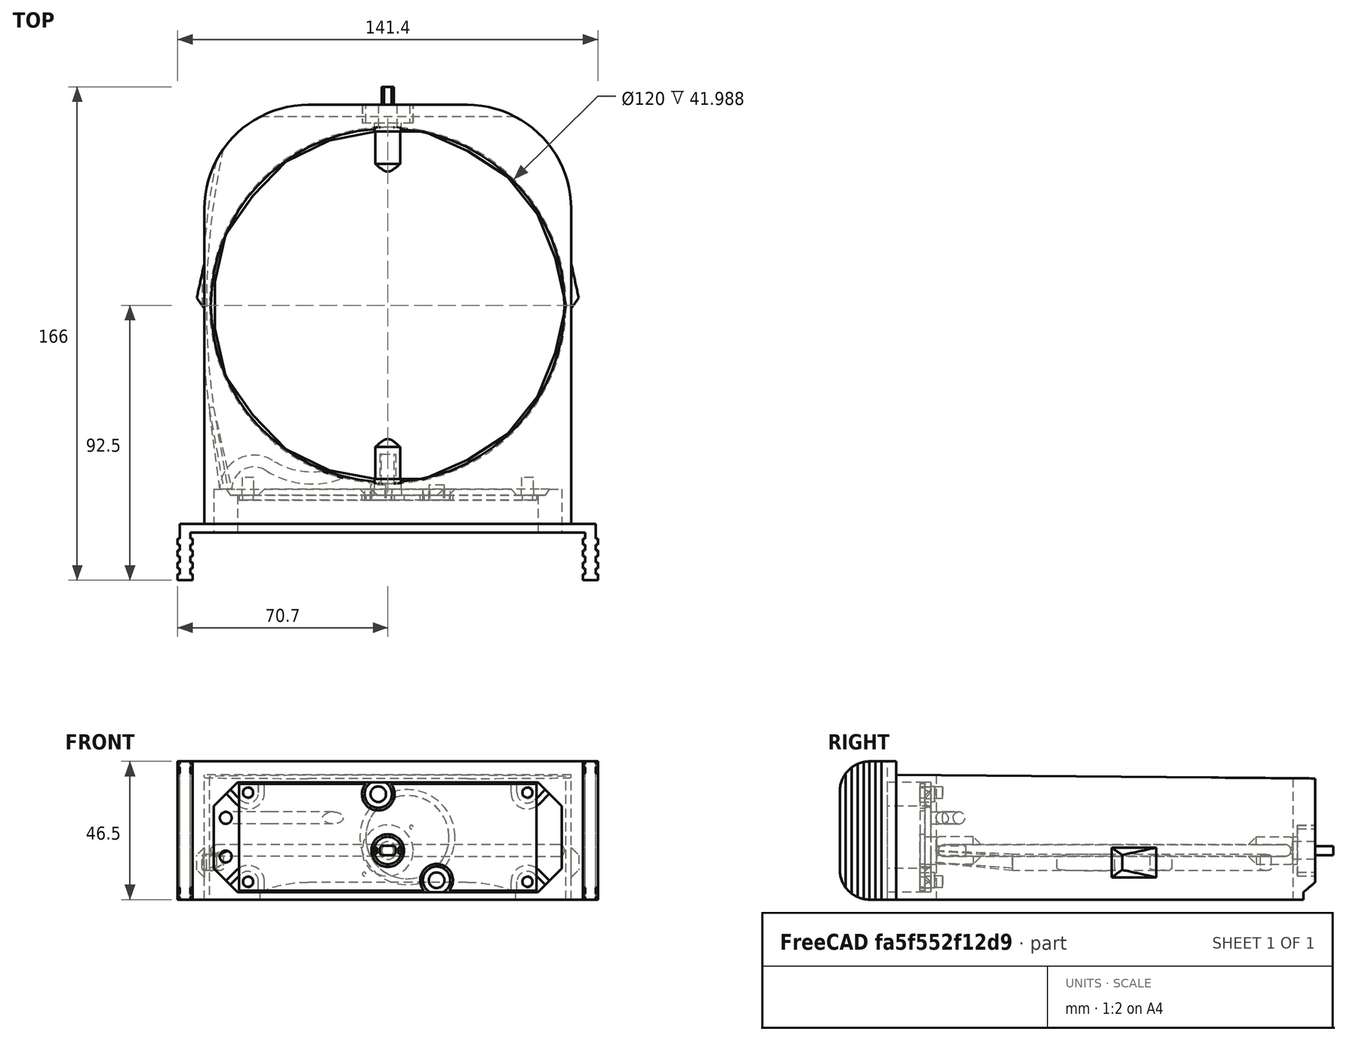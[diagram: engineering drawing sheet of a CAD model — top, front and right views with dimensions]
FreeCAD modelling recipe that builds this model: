
FCSTD DOCUMENT  (FreeCAD 0.20R27936 (Git))
Label: OpenDucoValve
License: All rights reserved
LicenseURL: http://en.wikipedia.org/wiki/All_rights_reserved
objects: Sketcher::SketchObject×26, TechDraw::DrawViewDimension×16, PartDesign::Pad×8, PartDesign::Pocket×8, PartDesign::Plane×5, PartDesign::Body×3, PartDesign::Line×2, PartDesign::Mirrored×2, PartDesign::SubtractivePipe×2, PartDesign::Fillet×2, PartDesign::Chamfer×2, Spreadsheet::Sheet×1, PartDesign::AdditiveLoft×1, PartDesign::SubtractiveLoft×1, TechDraw::DrawSVGTemplate×1, TechDraw::DrawViewPart×1, TechDraw::DrawPage×1
note: 86 computed .brp shape members not serialized (recipe doc carries the construction recipe); baked Part::Feature solids carry a one-line shape summary decoded from their .brp

FEATURE [Spreadsheet::Sheet] Spreadsheet
  cells = A1=Bearing Bore Size; B1(BearingBoreSize)=17.2; A2=Threaded Insert M4 Hole Size; B2(ThreadedInsertM4HoleSize)=5.25; C2=M4 X D6.0 X L5.0; A3=PCB Screw Hole Size; B3(ThreadedInsertM3HoleSize)=3.95; C3=M3 X D5.0 X L5.0; D3=3.95; A4=Motor Shaft Cutout Diameter; B4(MotorShaftCutoutDiameter)=5.4; A5=Motor Shaft Cutout Thickness; B5(MotorShaftCutoutThickness)=3.1; A6=Potentiometer Pin Diameter; B6(PotentiometerPinDiameter)=4; A7=Potentiometer Pin Thickness; B7(PotentiometerPinThickness)=3; A8=Bearing Inside Bore Size; B8(BearingInsideBoreSize)=6; A9=PCB Thickness; B9(PCBThickness)=1.6; C9=PCB Size 100x36; D9=Hole Square 94x30
FEATURE [Sketcher::SketchObject] Sketch
  FullyConstrained = true
  MapMode = 5
  Support = -> [XY_Plane]
  sketch-geometry (71):
    g0: Circle CenterX=0 CenterY=0 CenterZ=0 NormalX=0 NormalY=0 NormalZ=1 AngleXU=0 Radius=60
    g1: LineSegment StartX=-61.75 StartY=-73.5 StartZ=0 EndX=-61.75 EndY=32.5 EndZ=0
    g2: LineSegment StartX=61.75 StartY=-73.5 StartZ=0 EndX=61.75 EndY=32.5 EndZ=0
    g3: LineSegment StartX=26.75 StartY=67.5 StartZ=0 EndX=-26.75 EndY=67.5 EndZ=0
    g4: ArcOfCircle CenterX=-26.75 CenterY=32.5 CenterZ=0 NormalX=0 NormalY=0 NormalZ=1 AngleXU=0 Radius=35 StartAngle=1.5708 EndAngle=3.14159
    g5: ArcOfCircle CenterX=26.75 CenterY=32.5 CenterZ=0 NormalX=0 NormalY=0 NormalZ=1 AngleXU=0 Radius=35 StartAngle=0 EndAngle=1.5708
    g6: LineSegment StartX=-61.75 StartY=-73.5 StartZ=0 EndX=-70 EndY=-73.5 EndZ=0
    g7: LineSegment StartX=61.75 StartY=-73.5 StartZ=0 EndX=70 EndY=-73.5 EndZ=0
    g8: LineSegment StartX=-70 StartY=-73.5 StartZ=0 EndX=-70 EndY=-78.5 EndZ=0
    g9: LineSegment StartX=-70 StartY=-78.5 StartZ=0 EndX=-70.7 EndY=-78.5 EndZ=0
    g10: LineSegment StartX=-70.7 StartY=-78.5 StartZ=0 EndX=-70.7 EndY=-80.5 EndZ=0
    g11: LineSegment StartX=-70.7 StartY=-80.5 StartZ=0 EndX=-70 EndY=-80.5 EndZ=0
    g12: LineSegment StartX=-70 StartY=-80.5 StartZ=0 EndX=-70 EndY=-82.5 EndZ=0
    g13: LineSegment StartX=-70 StartY=-82.5 StartZ=0 EndX=-70.7 EndY=-82.5 EndZ=0
    g14: LineSegment StartX=-70.7 StartY=-82.5 StartZ=0 EndX=-70.7 EndY=-84.5 EndZ=0
    g15: LineSegment StartX=-70.7 StartY=-84.5 StartZ=0 EndX=-70 EndY=-84.5 EndZ=0
    g16: LineSegment StartX=-70 StartY=-84.5 StartZ=0 EndX=-70 EndY=-86.5 EndZ=0
    g17: LineSegment StartX=-70 StartY=-86.5 StartZ=0 EndX=-70.7 EndY=-86.5 EndZ=0
    g18: LineSegment StartX=-70.7 StartY=-86.5 StartZ=0 EndX=-70.7 EndY=-88.5 EndZ=0
    g19: LineSegment StartX=-70.7 StartY=-88.5 StartZ=0 EndX=-70 EndY=-88.5 EndZ=0
    g20: LineSegment StartX=-70 StartY=-88.5 StartZ=0 EndX=-70 EndY=-90.5 EndZ=0
    g21: LineSegment StartX=-70 StartY=-90.5 StartZ=0 EndX=-70.7 EndY=-90.5 EndZ=0
    g22: LineSegment StartX=-70.7 StartY=-90.5 StartZ=0 EndX=-70.7 EndY=-92.5 EndZ=0
    g23: LineSegment StartX=-70.7 StartY=-92.5 StartZ=0 EndX=-65.7 EndY=-92.5 EndZ=0
    g24: LineSegment StartX=-65.7 StartY=-92.5 StartZ=0 EndX=-65.7 EndY=-90.5 EndZ=0
    g25: LineSegment StartX=-65.7 StartY=-90.5 StartZ=0 EndX=-66.4 EndY=-90.5 EndZ=0
    g26: LineSegment StartX=-66.4 StartY=-90.5 StartZ=0 EndX=-66.4 EndY=-88.5 EndZ=0
    g27: LineSegment StartX=-66.4 StartY=-88.5 StartZ=0 EndX=-65.7 EndY=-88.5 EndZ=0
    g28: LineSegment StartX=-65.7 StartY=-88.5 StartZ=0 EndX=-65.7 EndY=-86.5 EndZ=0
    g29: LineSegment StartX=-65.7 StartY=-86.5 StartZ=0 EndX=-66.4 EndY=-86.5 EndZ=0
    g30: LineSegment StartX=-66.4 StartY=-86.5 StartZ=0 EndX=-66.4 EndY=-84.5 EndZ=0
    g31: LineSegment StartX=-66.4 StartY=-84.5 StartZ=0 EndX=-65.7 EndY=-84.5 EndZ=0
    g32: LineSegment StartX=-65.7 StartY=-84.5 StartZ=0 EndX=-65.7 EndY=-82.5 EndZ=0
    g33: LineSegment StartX=-65.7 StartY=-82.5 StartZ=0 EndX=-66.4 EndY=-82.5 EndZ=0
    g34: LineSegment StartX=-66.4 StartY=-82.5 StartZ=0 EndX=-66.4 EndY=-80.5 EndZ=0
    g35: LineSegment StartX=-66.4 StartY=-80.5 StartZ=0 EndX=-65.7 EndY=-80.5 EndZ=0
    g36: LineSegment StartX=-66.4 StartY=-76.5 StartZ=0 EndX=66.4 EndY=-76.5 EndZ=0
    g37: LineSegment StartX=-65.7 StartY=-80.5 StartZ=0 EndX=-65.7 EndY=-78.5 EndZ=0
    g38: LineSegment StartX=-65.7 StartY=-78.5 StartZ=0 EndX=-66.4 EndY=-78.5 EndZ=0
    g39: LineSegment StartX=-66.4 StartY=-78.5 StartZ=0 EndX=-66.4 EndY=-76.5 EndZ=0
    g40: LineSegment StartX=70 StartY=-73.5 StartZ=0 EndX=70 EndY=-78.5 EndZ=0
    g41: LineSegment StartX=70 StartY=-78.5 StartZ=0 EndX=70.7 EndY=-78.5 EndZ=0
    g42: LineSegment StartX=70.7 StartY=-78.5 StartZ=0 EndX=70.7 EndY=-80.5 EndZ=0
    g43: LineSegment StartX=70.7 StartY=-80.5 StartZ=0 EndX=70 EndY=-80.5 EndZ=0
    g44: LineSegment StartX=70 StartY=-80.5 StartZ=0 EndX=70 EndY=-82.5 EndZ=0
    g45: LineSegment StartX=70 StartY=-82.5 StartZ=0 EndX=70.7 EndY=-82.5 EndZ=0
    g46: LineSegment StartX=70.7 StartY=-82.5 StartZ=0 EndX=70.7 EndY=-84.5 EndZ=0
    g47: LineSegment StartX=70.7 StartY=-84.5 StartZ=0 EndX=70 EndY=-84.5 EndZ=0
    g48: LineSegment StartX=70 StartY=-84.5 StartZ=0 EndX=70 EndY=-86.5 EndZ=0
    g49: LineSegment StartX=70 StartY=-86.5 StartZ=0 EndX=70.7 EndY=-86.5 EndZ=0
    g50: LineSegment StartX=70.7 StartY=-86.5 StartZ=0 EndX=70.7 EndY=-88.5 EndZ=0
    g51: LineSegment StartX=70.7 StartY=-88.5 StartZ=0 EndX=70 EndY=-88.5 EndZ=0
    g52: LineSegment StartX=70 StartY=-88.5 StartZ=0 EndX=70 EndY=-90.5001 EndZ=0
    g53: LineSegment StartX=70 StartY=-90.5001 StartZ=0 EndX=70.7 EndY=-90.5001 EndZ=0
    g54: LineSegment StartX=70.7 StartY=-90.5001 StartZ=0 EndX=70.7 EndY=-92.5001 EndZ=0
    g55: LineSegment StartX=70.7 StartY=-92.5001 StartZ=0 EndX=65.7 EndY=-92.5001 EndZ=0
    g56: LineSegment StartX=65.7 StartY=-92.5001 StartZ=0 EndX=65.7 EndY=-90.5001 EndZ=0
    g57: LineSegment StartX=65.7 StartY=-90.5001 StartZ=0 EndX=66.4 EndY=-90.5001 EndZ=0
    g58: LineSegment StartX=66.4 StartY=-90.5001 StartZ=0 EndX=66.4 EndY=-88.5 EndZ=0
    g59: LineSegment StartX=66.4 StartY=-88.5 StartZ=0 EndX=65.7 EndY=-88.5 EndZ=0
    g60: LineSegment StartX=65.7 StartY=-88.5 StartZ=0 EndX=65.7 EndY=-86.5 EndZ=0
    g61: LineSegment StartX=65.7 StartY=-86.5 StartZ=0 EndX=66.4 EndY=-86.5 EndZ=0
    g62: LineSegment StartX=66.4 StartY=-86.5 StartZ=0 EndX=66.4 EndY=-84.5 EndZ=0
    g63: LineSegment StartX=66.4 StartY=-84.5 StartZ=0 EndX=65.7 EndY=-84.5 EndZ=0
    g64: LineSegment StartX=65.7 StartY=-84.5 StartZ=0 EndX=65.7 EndY=-82.5 EndZ=0
    g65: LineSegment StartX=65.7 StartY=-82.5 StartZ=0 EndX=66.4 EndY=-82.5 EndZ=0
    g66: LineSegment StartX=66.4 StartY=-82.5 StartZ=0 EndX=66.4 EndY=-80.5 EndZ=0
    g67: LineSegment StartX=66.4 StartY=-80.5 StartZ=0 EndX=65.7 EndY=-80.5 EndZ=0
    g68: LineSegment StartX=65.7 StartY=-80.5 StartZ=0 EndX=65.7 EndY=-78.5 EndZ=0
    g69: LineSegment StartX=65.7 StartY=-78.5 StartZ=0 EndX=66.4 EndY=-78.5 EndZ=0
    g70: LineSegment StartX=66.4 StartY=-78.5 StartZ=0 EndX=66.4 EndY=-76.5 EndZ=0
  constraints (207):
    c: Coincident(g0,g-1)
    c: Diameter(g0) = 120
    c: Vertical(g1)
    c: Vertical(g2)
    c: Tangent(g1,g4) = 1.5708
    c: Tangent(g3,g4) = -1.5708
    c: Tangent(g2,g5) = -1.5708
    c: Tangent(g3,g5) = -1.5708
    c: Radius(g5) = 35
    c: DistanceY(g0,g3) = 67.5
    c: Symmetric(g3,g3,g-2)
    c: DistanceX(g1,g2) = 123.5
    c: DistanceY(g1,g0) = 73.5
    c: Symmetric(g1,g2,g-2)
    c: Coincident(g6,g1)
    c: Horizontal(g6)
    c: Coincident(g7,g2)
    c: Horizontal(g7)
    c: Equal(g7,g6)
    c: DistanceX(g6,g7) = 140
    c: Coincident(g8,g6)
    c: Vertical(g8)
    c: Coincident(g9,g8)
    c: Horizontal(g9)
    c: Coincident(g10,g9)
    c: Vertical(g10)
    c: Coincident(g11,g10)
    c: Horizontal(g11)
    c: Coincident(g12,g11)
    c: Vertical(g12)
    c: Coincident(g13,g12)
    c: Horizontal(g13)
    c: Coincident(g14,g13)
    c: Vertical(g14)
    c: Coincident(g15,g14)
    c: Horizontal(g15)
    c: Coincident(g16,g15)
    c: Vertical(g16)
    c: Coincident(g17,g16)
    c: Horizontal(g17)
    c: Coincident(g18,g17)
    c: Vertical(g18)
    c: Coincident(g19,g18)
    c: Coincident(g20,g19)
    c: Vertical(g20)
    c: Coincident(g21,g20)
    c: Horizontal(g21)
    c: Coincident(g22,g21)
    c: Vertical(g22)
    c: Vertical(g8,g15)
    c: Vertical(g15,g19)
    c: Vertical(g9,g13)
    c: Vertical(g13,g17)
    c: Vertical(g17,g21)
    c: Equal(g22,g20)
    c: Equal(g20,g18)
    c: Equal(g18,g16)
    c: Equal(g16,g14)
    c: Equal(g14,g12)
    c: Equal(g12,g10)
    c: Equal(g19,g17)
    c: Equal(g15,g13)
    c: DistanceX(g9,g9) = 0.7
    c: DistanceY(g10,g10) = 2
    c: Coincident(g23,g22)
    c: Horizontal(g23)
    c: Coincident(g24,g23)
    c: Vertical(g24)
    c: Coincident(g25,g24)
    c: Horizontal(g25)
    c: Coincident(g26,g25)
    c: Vertical(g26)
    c: Coincident(g26,g27)
    c: Horizontal(g27)
    c: Coincident(g27,g28)
    c: Vertical(g28)
    c: Coincident(g28,g29)
    c: Horizontal(g29)
    c: Coincident(g29,g30)
    c: Vertical(g30)
    c: Coincident(g30,g31)
    c: Horizontal(g31)
    c: Coincident(g31,g32)
    c: Vertical(g32)
    c: Coincident(g32,g33)
    c: Horizontal(g33)
    c: Coincident(g33,g34)
    c: Vertical(g34)
    c: Coincident(g34,g35)
    c: Horizontal(g35)
    c: Horizontal(g21,g24)
    c: Horizontal(g27,g18)
    c: Horizontal(g28,g17)
    c: Horizontal(g31,g14)
    c: Horizontal(g32,g13)
    c: Horizontal(g35,g10)
    c: Vertical(g25,g29)
    c: Vertical(g29,g33)
    c: Vertical(g24,g27)
    c: Vertical(g27,g31)
    c: Vertical(g31,g35)
    c: Equal(g13,g33)
    c: DistanceX(g23,g23) = 5
    c: Symmetric(g36,g36,g-2)
    c: DistanceY(g36,g1) = 3
    c: Coincident(g35,g37)
    c: Vertical(g37)
    c: Coincident(g37,g38)
    c: Coincident(g38,g39)
    c: Coincident(g39,g36)
    c: Vertical(g39)
    c: Horizontal(g38)
    c: Vertical(g38,g34)
    c: Horizontal(g37,g8)
    c: Equal(g37,g39)
    c: Vertical(g40)
    c: Coincident(g41,g40)
    c: Horizontal(g41)
    c: Coincident(g42,g41)
    c: Vertical(g42)
    c: Coincident(g43,g42)
    c: Horizontal(g43)
    c: Coincident(g44,g43)
    c: Vertical(g44)
    c: Coincident(g45,g44)
    c: Horizontal(g45)
    c: Coincident(g46,g45)
    c: Vertical(g46)
    c: Coincident(g47,g46)
    c: Horizontal(g47)
    c: Coincident(g48,g47)
    c: Vertical(g48)
    c: Coincident(g49,g48)
    c: Horizontal(g49)
    c: Coincident(g50,g49)
    c: Vertical(g50)
    c: Coincident(g51,g50)
    c: Coincident(g52,g51)
    c: Vertical(g52)
    c: Coincident(g53,g52)
    c: Horizontal(g53)
    c: Coincident(g54,g53)
    c: Vertical(g54)
    c: Equal(g54,g52)
    c: Equal(g52,g50)
    c: Equal(g50,g48)
    c: Equal(g48,g46)
    c: Equal(g46,g44)
    c: Equal(g44,g42)
    c: Equal(g51,g49)
    c: Coincident(g55,g54)
    c: Horizontal(g55)
    c: Coincident(g56,g55)
    c: Vertical(g56)
    c: Coincident(g57,g56)
    c: Horizontal(g57)
    c: Coincident(g58,g57)
    c: Vertical(g58)
    c: Coincident(g58,g59)
    c: Horizontal(g59)
    c: Coincident(g59,g60)
    c: Vertical(g60)
    c: Coincident(g60,g61)
    c: Horizontal(g61)
    c: Coincident(g61,g62)
    c: Vertical(g62)
    c: Coincident(g62,g63)
    c: Horizontal(g63)
    c: Coincident(g63,g64)
    c: Vertical(g64)
    c: Coincident(g64,g65)
    c: Horizontal(g65)
    c: Coincident(g65,g66)
    c: Vertical(g66)
    c: Coincident(g66,g67)
    c: Horizontal(g67)
    c: Equal(g45,g65)
    c: Coincident(g67,g68)
    c: Vertical(g68)
    c: Coincident(g68,g69)
    c: Coincident(g69,g70)
    c: Vertical(g70)
    c: Horizontal(g69)
    c: Equal(g68,g70)
    c: Coincident(g70,g36)
    c: Equal(g58,g60)
    c: Equal(g60,g62)
    c: Equal(g62,g64)
    c: Equal(g64,g66)
    c: Equal(g66,g68)
    c: Equal(g70,g56)
    c: Equal(g56,g54)
    c: Equal(g69,g67)
    c: Equal(g67,g65)
    c: Equal(g65,g63)
    c: Equal(g63,g61)
    c: Equal(g61,g59)
    c: Equal(g59,g57)
    c: Equal(g57,g53)
    c: Equal(g53,g51)
    c: Equal(g49,g47)
    c: Equal(g45,g43)
    c: Equal(g43,g41)
    c: Coincident(g40,g7)
    c: Horizontal(g51)
    c: Equal(g63,g29)
    c: Equal(g56,g26)
FEATURE [PartDesign::Pad] Pad
  Direction = (0,0,1)
  Length = 46.5
  Length2 = 10
  Profile = -> Sketch
  ReferenceAxis = -> Sketch [N_Axis]
  Type = 0
FEATURE [Sketcher::SketchObject] Sketch001
  FullyConstrained = true
  MapMode = 5
  Placement = pos=(0,0,0) rot=(0.57735,0.57735,0.57735;2.0944rad)
  Support = -> [YZ_Plane]
  sketch-geometry (16):
    g0: LineSegment StartX=-73.5 StartY=46.5 StartZ=0 EndX=-73.5 EndY=42 EndZ=0
    g1: LineSegment StartX=-73.5 StartY=42 StartZ=0 EndX=67.5 EndY=40.7695 EndZ=0
    g2: LineSegment StartX=67.5 StartY=40.7695 StartZ=0 EndX=67.5 EndY=46.5 EndZ=0
    g3: LineSegment StartX=-73.5 StartY=46.5 StartZ=0 EndX=67.5 EndY=46.5 EndZ=0
    g4: LineSegment StartX=63.5 StartY=0 StartZ=0 EndX=63.5 EndY=2.5 EndZ=0
    g5: LineSegment StartX=63.5 StartY=2.5 StartZ=0 EndX=67.5 EndY=5.8564 EndZ=0
    g6: LineSegment StartX=67.5 StartY=5.8564 StartZ=0 EndX=67.5 EndY=0 EndZ=0
    g7: LineSegment StartX=67.5 StartY=0 StartZ=0 EndX=63.5 EndY=0 EndZ=0
    g8: ArcOfCircle CenterX=-82.5 CenterY=36.5 CenterZ=0 NormalX=0 NormalY=0 NormalZ=1 AngleXU=0 Radius=10 StartAngle=1.5708 EndAngle=3.14159
    g9: ArcOfCircle CenterX=-82.5 CenterY=10 CenterZ=0 NormalX=0 NormalY=0 NormalZ=1 AngleXU=0 Radius=10 StartAngle=3.14159 EndAngle=4.71239
    g10: LineSegment StartX=-92.5 StartY=36.5 StartZ=0 EndX=-92.5 EndY=10 EndZ=0
    g11: LineSegment StartX=-82.5 StartY=46.5 StartZ=0 EndX=-82.5 EndY=51 EndZ=0
    g12: LineSegment StartX=-82.5 StartY=51 StartZ=0 EndX=-223.5 EndY=51 EndZ=0
    g13: LineSegment StartX=-223.5 StartY=51 StartZ=0 EndX=-223.5 EndY=-4.5 EndZ=0
    g14: LineSegment StartX=-223.5 StartY=-4.5 StartZ=0 EndX=-82.5 EndY=-4.5 EndZ=0
    g15: LineSegment StartX=-82.5 StartY=-4.5 StartZ=0 EndX=-82.5 EndY=1.8e-15 EndZ=0
  constraints (50):
    c: Vertical(g0)
    c: Coincident(g1,g0)
    c: Coincident(g2,g1)
    c: Vertical(g2)
    c: Coincident(g3,g0)
    c: Coincident(g3,g2)
    c: DistanceY(g-1,g0) = 42
    c: DistanceX(g0,g-1) = 73.5
    c: Angle(g1,g0) = 1.57952
    c: DistanceY(g0,g0) = 4.5
    c: Horizontal(g3)
    c: DistanceX(g-1,g1) = 67.5
    c: PointOnObject(g4,g-1)
    c: Vertical(g4)
    c: Coincident(g5,g4)
    c: Coincident(g6,g5)
    c: PointOnObject(g6,g-1)
    c: Vertical(g6)
    c: Coincident(g7,g6)
    c: Coincident(g7,g4)
    c: Vertical(g1,g5)
    c: DistanceX(g7,g7) = 4
    c: Angle(g5,g6) = 0.872665
    c: DistanceY(g4,g4) = 2.5
    c: Horizontal(g8,g8)
    c: Horizontal(g9,g9)
    c: Vertical(g9,g9)
    c: Vertical(g9,g8)
    c: Vertical(g8,g8)
    c: Radius(g8) = 10
    c: Horizontal(g8,g0)
    c: Horizontal(g-1,g9)
    c: DistanceX(g9,g-1) = 92.5
    c: Vertical(g8,g9)
    c: Coincident(g10,g8)
    c: Coincident(g10,g9)
    c: Coincident(g11,g8)
    c: Vertical(g11)
    c: Coincident(g12,g11)
    c: Horizontal(g12)
    c: Coincident(g13,g12)
    c: Vertical(g13)
    c: Coincident(g14,g13)
    c: Horizontal(g14)
    c: Coincident(g15,g14)
    c: Coincident(g15,g9)
    c: Vertical(g15)
    c: Equal(g15,g11)
    c: Equal(g11,g0)
    c: Equal(g3,g12)
FEATURE [PartDesign::Pocket] Pocket
  BaseFeature = -> Pad
  Direction = (-1,2e-16,-3e-16)
  Length = 5
  Length2 = 5
  Midplane = true
  Profile = -> Sketch001
  ReferenceAxis = -> Sketch001 [N_Axis]
  Type = 1
FEATURE [PartDesign::Line] DatumLine
  AttacherType = Attacher::AttachEngineLine
  AttachmentOffset = pos=(0,16.5,0) rot=(0,0,1;0rad)
  Length = 20
  MapMode = 29
  Placement = pos=(0,3.7e-15,16.5) rot=(0,0.707107,0.707107;3.14159rad)
  ResizeMode = 0
  Support = -> [Y_Axis]
FEATURE [PartDesign::Plane] DatumPlane
  AttachmentOffset = pos=(0,0,67.5) rot=(0,0,1;0rad)
  Length = 94.829
  MapMode = 5
  Placement = pos=(0,67.5,1.5e-14) rot=(0,0.707107,0.707107;3.14159rad)
  ResizeMode = 0
  Support = -> [XZ_Plane]
  Width = 67.8292
FEATURE [Sketcher::SketchObject] Sketch002
  ExternalGeometry = -> [DatumLine]
  FullyConstrained = true
  MapMode = 5
  Placement = pos=(0,67.5,1.5e-14) rot=(0,0.707107,0.707107;3.14159rad)
  Support = -> [DatumPlane]
  sketch-geometry (1):
    g0: Circle CenterX=0 CenterY=16.5 CenterZ=0 NormalX=0 NormalY=0 NormalZ=1 AngleXU=0 Radius=4.6
  constraints (2):
    c: Coincident(g0,g-3)
    c: Diameter(g0) = 9.2
FEATURE [PartDesign::Pocket] Pocket001
  BaseFeature = -> Pocket
  Direction = (0,-1,-2e-16)
  Length = 6
  Length2 = 5
  Profile = -> Sketch002
  ReferenceAxis = -> Sketch002 [N_Axis]
  Type = 1
FEATURE [Sketcher::SketchObject] Sketch003
  ExternalGeometry = -> [DatumLine]
  FullyConstrained = true
  MapMode = 5
  Placement = pos=(0,67.5,1.5e-14) rot=(0,0.707107,0.707107;3.14159rad)
  Support = -> [DatumPlane]
  expr: Constraints[1] = Spreadsheet.BearingBoreSize
  sketch-geometry (1):
    g0: Circle CenterX=0 CenterY=16.5 CenterZ=0 NormalX=0 NormalY=0 NormalZ=1 AngleXU=0 Radius=8.6
  constraints (2):
    c: Coincident(g0,g-3)
    c: Diameter(g0) = 17.2
FEATURE [PartDesign::Pocket] Pocket002
  BaseFeature = -> Pocket001
  Direction = (0,-1,-2e-16)
  Length = 6
  Length2 = 5
  Profile = -> Sketch003
  ReferenceAxis = -> Sketch003 [N_Axis]
  Type = 0
FEATURE [Sketcher::SketchObject] Sketch004
  ExternalGeometry = -> [DatumLine]
  FullyConstrained = true
  MapMode = 5
  Placement = pos=(0,67.5,1.5e-14) rot=(0,0.707107,0.707107;3.14159rad)
  Support = -> [DatumPlane]
  sketch-geometry (3):
    g0: Circle CenterX=-7.9196 CenterY=24.4196 CenterZ=0 NormalX=0 NormalY=0 NormalZ=1 AngleXU=0 Radius=0.6
    g1: Circle CenterX=7.9196 CenterY=8.5804 CenterZ=0 NormalX=0 NormalY=0 NormalZ=1 AngleXU=0 Radius=0.6
    g2: LineSegment StartX=-7.9196 StartY=24.4196 StartZ=0 EndX=0 EndY=16.5 EndZ=0
  constraints (7):
    c: Symmetric(g0,g1,g-3)
    c: Distance(g0,g1) = 22.4
    c: Coincident(g2,g0)
    c: Coincident(g2,g-3)
    c: Angle(g2,g-2) = 2.35619
    c: Diameter(g1) = 1.2
    c: Equal(g1,g0)
FEATURE [PartDesign::Pocket] Pocket003
  BaseFeature = -> Pocket002
  Direction = (0,-1,-2e-16)
  Length = 6
  Length2 = 5
  Profile = -> Sketch004
  ReferenceAxis = -> Sketch004 [N_Axis]
  Type = 0
FEATURE [PartDesign::Plane] DatumPlane001  label="FrontPlane"
  AttachmentOffset = pos=(0,0,61.9) rot=(0,0,1;0rad)
  Length = 94.829
  MapMode = 5
  Placement = pos=(0,-61.9,-1.37e-14) rot=(1,0,0;1.5708rad)
  ResizeMode = 0
  Support = -> [XZ_Plane]
  Width = 67.8292
FEATURE [Sketcher::SketchObject] Sketch006  label="FrontSketch"
  ExternalGeometry = -> [DatumLine]
  FullyConstrained = true
  MapMode = 5
  Placement = pos=(0,-61.9,-1.37e-14) rot=(1,0,0;1.5708rad)
  Support = -> [DatumPlane001]
  expr: Constraints[37] = Spreadsheet.ThreadedInsertM4HoleSize
  expr: Constraints[87] = Spreadsheet.ThreadedInsertM3HoleSize
  sketch-geometry (50):
    g0: LineSegment StartX=-4.48751 StartY=23.1229 StartZ=0 EndX=4.48751 EndY=9.87714 EndZ=0
    g1: LineSegment StartX=4.48751 StartY=9.87714 StartZ=0 EndX=26.0118 EndY=24.4615 EndZ=0
    g2: LineSegment StartX=26.0118 StartY=24.4615 StartZ=0 EndX=17.0368 EndY=37.7073 EndZ=0
    g3: LineSegment StartX=17.0368 StartY=37.7073 StartZ=0 EndX=-4.48751 EndY=23.1229 EndZ=0
    g4: LineSegment StartX=-3.19356 StartY=35.475 StartZ=0 EndX=16.4393 EndY=6.5 EndZ=0
    g5: LineSegment StartX=0 StartY=16.5 StartZ=0 EndX=6.62286 EndY=20.9875 EndZ=0
    g6: Circle CenterX=-3.19356 CenterY=35.475 CenterZ=0 NormalX=0 NormalY=0 NormalZ=1 AngleXU=0 Radius=4
    g7: Circle CenterX=16.4393 CenterY=6.5 CenterZ=0 NormalX=0 NormalY=0 NormalZ=1 AngleXU=0 Radius=4
    g8: LineSegment StartX=-50.5 StartY=39.5 StartZ=0 EndX=50.5 EndY=39.5 EndZ=0
    g9: LineSegment StartX=50.5 StartY=39.5 StartZ=0 EndX=50.5 EndY=2.5 EndZ=0
    g10: LineSegment StartX=50.5 StartY=2.5 StartZ=0 EndX=-50.5 EndY=2.5 EndZ=0
    g11: LineSegment StartX=-50.5 StartY=2.5 StartZ=0 EndX=-50.5 EndY=39.5 EndZ=0
    g12: Circle CenterX=6.62286 CenterY=20.9875 CenterZ=0 NormalX=0 NormalY=0 NormalZ=1 AngleXU=0 Radius=14
    g13: Circle CenterX=-3.19356 CenterY=35.475 CenterZ=0 NormalX=0 NormalY=0 NormalZ=1 AngleXU=0 Radius=2.625
    g14: Circle CenterX=16.4393 CenterY=6.5 CenterZ=0 NormalX=0 NormalY=0 NormalZ=1 AngleXU=0 Radius=2.625
    g15: Circle CenterX=-3.19356 CenterY=35.475 CenterZ=0 NormalX=0 NormalY=0 NormalZ=1 AngleXU=0 Radius=4.6
    g16: Circle CenterX=16.4393 CenterY=6.5 CenterZ=0 NormalX=0 NormalY=0 NormalZ=1 AngleXU=0 Radius=4.6
    g17: LineSegment StartX=-7.79356 StartY=35.475 StartZ=0 EndX=-7.79356 EndY=39.5 EndZ=0
    g18: LineSegment StartX=1.40644 StartY=35.475 StartZ=0 EndX=1.40644 EndY=39.5 EndZ=0
    g19: LineSegment StartX=11.8393 StartY=6.5 StartZ=0 EndX=11.8393 EndY=2.5 EndZ=0
    g20: LineSegment StartX=21.0393 StartY=6.5 StartZ=0 EndX=21.0393 EndY=2.5 EndZ=0
    g21: Circle CenterX=-47 CenterY=36 CenterZ=0 NormalX=0 NormalY=0 NormalZ=1 AngleXU=0 Radius=3.5
    g22: Circle CenterX=-47 CenterY=6 CenterZ=0 NormalX=0 NormalY=0 NormalZ=1 AngleXU=0 Radius=3.5
    g23: Circle CenterX=47 CenterY=36 CenterZ=0 NormalX=0 NormalY=0 NormalZ=1 AngleXU=0 Radius=3.5
    g24: Circle CenterX=47 CenterY=6 CenterZ=0 NormalX=0 NormalY=0 NormalZ=1 AngleXU=0 Radius=3.5
    g25: LineSegment StartX=-43.5 StartY=36 StartZ=0 EndX=-43.5 EndY=39.5 EndZ=0
    g26: LineSegment StartX=-43.5 StartY=6 StartZ=0 EndX=-43.5 EndY=2.5 EndZ=0
    g27: LineSegment StartX=43.5 StartY=6 StartZ=0 EndX=43.5 EndY=2.5 EndZ=0
    g28: LineSegment StartX=43.5 StartY=36 StartZ=0 EndX=43.5 EndY=39.5 EndZ=0
    g29: Circle CenterX=-47 CenterY=36 CenterZ=0 NormalX=0 NormalY=0 NormalZ=1 AngleXU=0 Radius=1.975
    g30: Circle CenterX=-47 CenterY=6 CenterZ=0 NormalX=0 NormalY=0 NormalZ=1 AngleXU=0 Radius=1.975
    g31: Circle CenterX=47 CenterY=6 CenterZ=0 NormalX=0 NormalY=0 NormalZ=1 AngleXU=0 Radius=1.975
    g32: Circle CenterX=47 CenterY=36 CenterZ=0 NormalX=0 NormalY=0 NormalZ=1 AngleXU=0 Radius=1.975
    g33: Circle CenterX=0 CenterY=16.5 CenterZ=0 NormalX=0 NormalY=0 NormalZ=1 AngleXU=0 Radius=4.6
    g34: LineSegment StartX=-50.5 StartY=39.5 StartZ=0 EndX=-58.5 EndY=31.5 EndZ=0
    g35: LineSegment StartX=-58.5 StartY=31.5 StartZ=0 EndX=-58.5 EndY=10.5 EndZ=0
    g36: LineSegment StartX=-58.5 StartY=10.5 StartZ=0 EndX=-50.5 EndY=2.5 EndZ=0
    g37: LineSegment StartX=-52.9749 StartY=4.97487 StartZ=0 EndX=-49.4749 EndY=8.47487 EndZ=0
    g38: LineSegment StartX=-52.9749 StartY=37.0251 StartZ=0 EndX=-49.4749 EndY=33.5251 EndZ=0
    g39: LineSegment StartX=50.5 StartY=2.5 StartZ=0 EndX=58.5 EndY=10.5 EndZ=0
    g40: LineSegment StartX=58.5 StartY=10.5 StartZ=0 EndX=58.5 EndY=31.5 EndZ=0
    g41: LineSegment StartX=58.5 StartY=31.5 StartZ=0 EndX=50.5 EndY=39.5 EndZ=0
    g42: LineSegment StartX=52.9749 StartY=37.0251 StartZ=0 EndX=49.4749 EndY=33.5251 EndZ=0
    g43: LineSegment StartX=52.9749 StartY=4.97487 StartZ=0 EndX=49.4749 EndY=8.47487 EndZ=0
    g44: Circle CenterX=-54.5 CenterY=27.5 CenterZ=0 NormalX=0 NormalY=0 NormalZ=1 AngleXU=0 Radius=2
    g45: Circle CenterX=-54.5 CenterY=14.5 CenterZ=0 NormalX=0 NormalY=0 NormalZ=1 AngleXU=0 Radius=2
    g46: LineSegment StartX=-54.5 StartY=27.5 StartZ=0 EndX=-58.5 EndY=31.5 EndZ=0
    g47: LineSegment StartX=-54.5 StartY=14.5 StartZ=0 EndX=-58.5 EndY=10.5 EndZ=0
    g48: Circle CenterX=54.5 CenterY=27.5 CenterZ=0 NormalX=0 NormalY=0 NormalZ=1 AngleXU=0 Radius=2
    g49: Circle CenterX=54.5 CenterY=14.5 CenterZ=0 NormalX=0 NormalY=0 NormalZ=1 AngleXU=0 Radius=2
  constraints (135):
    c: Coincident(g1,g0)
    c: Coincident(g3,g0)
    c: Parallel(g3,g1)
    c: Coincident(g2,g3)
    c: Coincident(g2,g1)
    c: Parallel(g2,g0)
    c: Perpendicular(g0,g1)
    c: Distance(g0,g2) = 26
    c: Distance(g0,g0) = 16
    c: Symmetric(g0,g0,g-3)
    c: Parallel(g0,g4)
    c: Distance(g4,g4) = 35
    c: Coincident(g5,g-3)
    c: Perpendicular(g4,g5)
    c: Symmetric(g4,g4,g5)
    c: Coincident(g6,g4)
    c: Coincident(g7,g4)
    c: Diameter(g6) = 8
    c: Equal(g6,g7)
    c: Distance(g5,g5) = 8
    c: Coincident(g8,g9)
    c: Coincident(g9,g10)
    c: Coincident(g10,g11)
    c: Coincident(g11,g8)
    c: Horizontal(g8)
    c: Vertical(g9)
    c: Vertical(g11)
    c: DistanceY(g9,g9) = 37
    c: DistanceX(g8,g8) = 101
    c: Symmetric(g10,g9,g-2)
    c: DistanceY(g-1,g9) = 2.5
    c: Coincident(g12,g5)
    c: Diameter(g12) = 28
    c: Coincident(g13,g4)
    c: Coincident(g14,g4)
    c: Tangent(g10,g7)
    c: Equal(g13,g14)
    c: Diameter(g13) = 5.25
    c: Coincident(g15,g4)
    c: Coincident(g16,g4)
    c: Equal(g16,g15)
    c: Diameter(g16) = 9.2
    c: Vertical(g17)
    c: Vertical(g18)
    c: Tangent(g17,g15) = 1.5708
    c: Tangent(g18,g15) = -1.5708
    c: PointOnObject(g17,g8)
    c: PointOnObject(g18,g8)
    c: PointOnObject(g19,g10)
    c: Vertical(g19)
    c: PointOnObject(g20,g10)
    c: Vertical(g20)
    c: Tangent(g19,g16) = -1.5708
    c: Tangent(g20,g16) = 1.5708
    c: Tangent(g21,g11)
    c: Tangent(g21,g8)
    c: Diameter(g21) = 7
    c: Equal(g21,g22)
    c: Equal(g22,g24)
    c: Equal(g24,g23)
    c: Tangent(g22,g10)
    c: Horizontal(g22,g24)
    c: Horizontal(g23,g21)
    c: Tangent(g23,g9)
    c: Vertical(g24,g23)
    c: Vertical(g22,g21)
    c: PointOnObject(g25,g21)
    c: PointOnObject(g25,g8)
    c: Vertical(g25)
    c: Tangent(g25,g21)
    c: PointOnObject(g26,g22)
    c: PointOnObject(g26,g10)
    c: Vertical(g26)
    c: Tangent(g26,g22)
    c: PointOnObject(g27,g10)
    c: Vertical(g27)
    c: Tangent(g27,g24) = -1.5708
    c: PointOnObject(g28,g8)
    c: Vertical(g28)
    c: Tangent(g28,g23) = 1.5708
    c: Coincident(g29,g21)
    c: Coincident(g30,g22)
    c: Coincident(g31,g24)
    c: Coincident(g32,g23)
    c: Equal(g32,g31)
    c: Equal(g31,g29)
    c: Equal(g29,g30)
    c: Diameter(g29) = 3.95
    c: Coincident(g33,g5)
    c: Diameter(g33) = 9.2
    c: Coincident(g34,g8)
    c: Coincident(g35,g34)
    c: Vertical(g35)
    c: Coincident(g36,g35)
    c: Coincident(g36,g10)
    c: DistanceX(g34,g8) = 8
    c: Angle(g35,g34) = 2.35619
    c: Equal(g36,g34)
    c: PointOnObject(g37,g36)
    c: Tangent(g37,g22) = 1.5708
    c: Perpendicular(g37,g36)
    c: PointOnObject(g38,g34)
    c: PointOnObject(g38,g21)
    c: Tangent(g38,g21)
    c: Perpendicular(g34,g38)
    c: Coincident(g39,g9)
    c: Coincident(g40,g39)
    c: Vertical(g40)
    c: Coincident(g41,g40)
    c: Coincident(g41,g8)
    c: DistanceX(g8,g40) = 8
    c: Equal(g35,g40)
    c: Equal(g39,g41)
    c: PointOnObject(g42,g41)
    c: PointOnObject(g42,g23)
    c: Tangent(g42,g23)
    c: Perpendicular(g41,g42)
    c: PointOnObject(g43,g39)
    c: PointOnObject(g43,g24)
    c: Tangent(g43,g24)
    c: Perpendicular(g39,g43)
    c: Vertical(g45,g44)
    c: Diameter(g45) = 4
    c: Equal(g44,g45)
    c: DistanceX(g34,g44) = 4
    c: Coincident(g46,g44)
    c: Coincident(g46,g34)
    c: Coincident(g47,g45)
    c: Coincident(g47,g35)
    c: Equal(g47,g46)
    c: Perpendicular(g47,g36)
    c: Equal(g44,g48)
    c: Equal(g48,g49)
    c: Symmetric(g48,g44,g-2)
    c: Symmetric(g49,g45,g-2)
FEATURE [Sketcher::SketchObject] Sketch007
  ExternalGeometry = -> [Sketch006]
  FullyConstrained = true
  MapMode = 5
  Placement = pos=(0,-61.9,-1.37e-14) rot=(1,0,0;1.5708rad)
  Support = -> [DatumPlane001]
  sketch-geometry (8):
    g0: LineSegment StartX=-58.5 StartY=31.5 StartZ=0 EndX=-50.5 EndY=39.5 EndZ=0
    g1: LineSegment StartX=-50.5 StartY=39.5 StartZ=0 EndX=50.5 EndY=39.5 EndZ=0
    g2: LineSegment StartX=50.5 StartY=39.5 StartZ=0 EndX=58.5 EndY=31.5 EndZ=0
    g3: LineSegment StartX=58.5 StartY=31.5 StartZ=0 EndX=58.5 EndY=10.5 EndZ=0
    g4: LineSegment StartX=58.5 StartY=10.5 StartZ=0 EndX=50.5 EndY=2.5 EndZ=0
    g5: LineSegment StartX=50.5 StartY=2.5 StartZ=0 EndX=-50.5 EndY=2.5 EndZ=0
    g6: LineSegment StartX=-50.5 StartY=2.5 StartZ=0 EndX=-58.5 EndY=10.5 EndZ=0
    g7: LineSegment StartX=-58.5 StartY=10.5 StartZ=0 EndX=-58.5 EndY=31.5 EndZ=0
  constraints (16):
    c: Coincident(g-5,g0)
    c: Coincident(g0,g-3)
    c: Coincident(g0,g1)
    c: Coincident(g1,g-3)
    c: Coincident(g1,g2)
    c: Coincident(g2,g-6)
    c: Coincident(g2,g3)
    c: Coincident(g3,g-6)
    c: Coincident(g3,g4)
    c: Coincident(g4,g-4)
    c: Coincident(g4,g5)
    c: Coincident(g5,g-4)
    c: Coincident(g5,g6)
    c: Coincident(g6,g-5)
    c: Coincident(g6,g7)
    c: Coincident(g7,g0)
FEATURE [PartDesign::Pocket] Pocket004
  BaseFeature = -> Pocket003
  Direction = (0,1,2e-16)
  Length = 5
  Length2 = 5
  Profile = -> Sketch007
  ReferenceAxis = -> Sketch007 [N_Axis]
  Reversed = true
  Type = 1
FEATURE [Sketcher::SketchObject] Sketch008
  ExternalGeometry = -> [Sketch006]
  FullyConstrained = true
  MapMode = 5
  Placement = pos=(0,-61.9,-1.37e-14) rot=(1,0,0;1.5708rad)
  Support = -> [DatumPlane001]
  sketch-geometry (26):
    g0: ArcOfCircle CenterX=-47 CenterY=6 CenterZ=0 NormalX=0 NormalY=0 NormalZ=1 AngleXU=0 Radius=3.5 StartAngle=9.17263e-08 EndAngle=2.35619
    g1: ArcOfCircle CenterX=-47 CenterY=36 CenterZ=0 NormalX=0 NormalY=0 NormalZ=1 AngleXU=0 Radius=3.5 StartAngle=3.92699 EndAngle=6.28319
    g2: ArcOfCircle CenterX=47 CenterY=36 CenterZ=0 NormalX=0 NormalY=0 NormalZ=1 AngleXU=0 Radius=3.5 StartAngle=3.14159 EndAngle=5.49779
    g3: ArcOfCircle CenterX=47 CenterY=6 CenterZ=0 NormalX=0 NormalY=0 NormalZ=1 AngleXU=0 Radius=3.5 StartAngle=0.785398 EndAngle=3.14159
    g4: Circle CenterX=0 CenterY=16.5 CenterZ=0 NormalX=0 NormalY=0 NormalZ=1 AngleXU=0 Radius=4.6
    g5: Circle CenterX=6.62286 CenterY=20.9875 CenterZ=0 NormalX=0 NormalY=0 NormalZ=1 AngleXU=0 Radius=14
    g6: Circle CenterX=-47 CenterY=6 CenterZ=0 NormalX=0 NormalY=0 NormalZ=1 AngleXU=0 Radius=1.975
    g7: Circle CenterX=-47 CenterY=36 CenterZ=0 NormalX=0 NormalY=0 NormalZ=1 AngleXU=0 Radius=1.975
    g8: Circle CenterX=47 CenterY=36 CenterZ=0 NormalX=0 NormalY=0 NormalZ=1 AngleXU=0 Radius=1.975
    g9: Circle CenterX=47 CenterY=6 CenterZ=0 NormalX=0 NormalY=0 NormalZ=1 AngleXU=0 Radius=1.975
    g10: LineSegment StartX=-49.4749 StartY=33.5251 StartZ=0 EndX=-52.9749 EndY=37.0251 EndZ=0
    g11: LineSegment StartX=-52.9749 StartY=37.0251 StartZ=0 EndX=-50.5 EndY=39.5 EndZ=0
    g12: LineSegment StartX=-50.5 StartY=39.5 StartZ=0 EndX=-43.5 EndY=39.5 EndZ=0
    g13: LineSegment StartX=-43.5 StartY=39.5 StartZ=0 EndX=-43.5 EndY=36 EndZ=0
    g14: LineSegment StartX=-49.4749 StartY=8.47487 StartZ=0 EndX=-52.9749 EndY=4.97487 EndZ=0
    g15: LineSegment StartX=-52.9749 StartY=4.97487 StartZ=0 EndX=-50.5 EndY=2.5 EndZ=0
    g16: LineSegment StartX=-50.5 StartY=2.5 StartZ=0 EndX=-43.5 EndY=2.5 EndZ=0
    g17: LineSegment StartX=-43.5 StartY=2.5 StartZ=0 EndX=-43.5 EndY=6 EndZ=0
    g18: LineSegment StartX=49.4749 StartY=8.47487 StartZ=0 EndX=52.9749 EndY=4.97487 EndZ=0
    g19: LineSegment StartX=52.9749 StartY=4.97487 StartZ=0 EndX=50.5 EndY=2.5 EndZ=0
    g20: LineSegment StartX=50.5 StartY=2.5 StartZ=0 EndX=43.5 EndY=2.5 EndZ=0
    g21: LineSegment StartX=43.5 StartY=2.5 StartZ=0 EndX=43.5 EndY=6 EndZ=0
    g22: LineSegment StartX=43.5 StartY=36 StartZ=0 EndX=43.5 EndY=39.5 EndZ=0
    g23: LineSegment StartX=43.5 StartY=39.5 StartZ=0 EndX=50.5 EndY=39.5 EndZ=0
    g24: LineSegment StartX=50.5 StartY=39.5 StartZ=0 EndX=52.9749 EndY=37.0251 EndZ=0
    g25: LineSegment StartX=52.9749 StartY=37.0251 StartZ=0 EndX=49.4749 EndY=33.5251 EndZ=0
  constraints (52):
    c: Coincident(g2,g-9)
    c: Coincident(g2,g-18)
    c: Coincident(g3,g-10)
    c: Coincident(g3,g-12)
    c: Coincident(g4,g-6)
    c: Coincident(g5,g-5)
    c: Equal(g-5,g5)
    c: Equal(g-6,g4)
    c: Coincident(g6,g0)
    c: Coincident(g7,g1)
    c: Coincident(g8,g2)
    c: Coincident(g9,g3)
    c: Equal(g9,g-10)
    c: Equal(g8,g-9)
    c: Equal(g7,g-8)
    c: Equal(g6,g-7)
    c: Coincident(g10,g-15)
    c: Coincident(g11,g10)
    c: Coincident(g11,g-3)
    c: Coincident(g12,g11)
    c: Coincident(g12,g-16)
    c: Coincident(g13,g12)
    c: Coincident(g13,g1)
    c: Coincident(g14,g-14)
    c: Coincident(g15,g14)
    c: Coincident(g15,g-4)
    c: Coincident(g16,g15)
    c: Coincident(g16,g-13)
    c: Coincident(g17,g16)
    c: Coincident(g17,g0)
    c: Coincident(g18,g-11)
    c: Coincident(g19,g18)
    c: Coincident(g19,g-4)
    c: Coincident(g20,g19)
    c: Coincident(g20,g-12)
    c: Coincident(g21,g20)
    c: Coincident(g21,g3)
    c: Coincident(g22,g2)
    c: Coincident(g22,g-18)
    c: Coincident(g23,g22)
    c: Coincident(g23,g-3)
    c: Coincident(g24,g23)
    c: Coincident(g24,g-17)
    c: Coincident(g25,g24)
    c: Coincident(g-13,g0)
    c: Coincident(g0,g-7)
    c: Tangent(g14,g0) = -1.5708
    c: Coincident(g-8,g1)
    c: Coincident(g1,g-16)
    c: Tangent(g10,g1) = 1.5708
    c: Tangent(g25,g2) = 1.5708
    c: Tangent(g18,g3) = 1.5708
FEATURE [PartDesign::Pad] Pad001
  BaseFeature = -> Pocket004
  Direction = (0,-1,-2e-16)
  Length = 2
  Length2 = 10
  Profile = -> Sketch008
  ReferenceAxis = -> Sketch008 [N_Axis]
  Type = 0
FEATURE [Sketcher::SketchObject] Sketch009
  ExternalGeometry = -> [Sketch006]
  FullyConstrained = true
  MapMode = 5
  Placement = pos=(0,-61.9,-1.37e-14) rot=(1,0,0;1.5708rad)
  Support = -> [DatumPlane001]
  sketch-geometry (6):
    g0: ArcOfCircle CenterX=-3.19356 CenterY=35.475 CenterZ=0 NormalX=0 NormalY=0 NormalZ=1 AngleXU=0 Radius=4.6 StartAngle=2.07616 EndAngle=7.34861
    g1: LineSegment StartX=-5.42055 StartY=39.5 StartZ=0 EndX=-0.96657 EndY=39.5 EndZ=0
    g2: ArcOfCircle CenterX=16.4393 CenterY=6.5 CenterZ=0 NormalX=0 NormalY=0 NormalZ=1 AngleXU=0 Radius=4.6 StartAngle=5.22886 EndAngle=10.4791
    g3: LineSegment StartX=18.7108 StartY=2.5 StartZ=0 EndX=14.1677 EndY=2.5 EndZ=0
    g4: Circle CenterX=-3.19356 CenterY=35.475 CenterZ=0 NormalX=0 NormalY=0 NormalZ=1 AngleXU=0 Radius=2.625
    g5: Circle CenterX=16.4393 CenterY=6.5 CenterZ=0 NormalX=0 NormalY=0 NormalZ=1 AngleXU=0 Radius=2.625
  constraints (16):
    c: Coincident(g0,g-6)
    c: PointOnObject(g0,g-6)
    c: PointOnObject(g0,g-7)
    c: Coincident(g1,g0)
    c: Coincident(g1,g0)
    c: Horizontal(g1)
    c: Coincident(g2,g-5)
    c: PointOnObject(g2,g-5)
    c: PointOnObject(g2,g-8)
    c: Coincident(g3,g2)
    c: Coincident(g3,g2)
    c: Horizontal(g3)
    c: Coincident(g4,g0)
    c: Equal(g4,g-3)
    c: Coincident(g5,g2)
    c: Equal(g5,g-4)
FEATURE [PartDesign::Pad] Pad002
  BaseFeature = -> Pad001
  Direction = (0,-1,-2e-16)
  Length = 3.6
  Length2 = 10
  Profile = -> Sketch009
  ReferenceAxis = -> Sketch009 [N_Axis]
  Type = 0
  expr: Length = Spreadsheet.PCBThickness + 2
FEATURE [Sketcher::SketchObject] Sketch010
  ExternalGeometry = -> [Sketch006]
  FullyConstrained = false
  MapMode = 5
  Placement = pos=(0,-61.9,-1.37e-14) rot=(1,0,0;1.5708rad)
  Support = -> [DatumPlane001]
  sketch-geometry (3):
    g0: Circle CenterX=-3.19356 CenterY=35.475 CenterZ=0 NormalX=0 NormalY=0 NormalZ=1 AngleXU=0 Radius=2.625
    g1: Circle CenterX=16.4393 CenterY=6.5 CenterZ=0 NormalX=0 NormalY=0 NormalZ=1 AngleXU=0 Radius=2.625
    g2: Circle CenterX=0 CenterY=16.5 CenterZ=0 NormalX=0 NormalY=0 NormalZ=1 AngleXU=0 Radius=4.6
  constraints (1):
    c: Equal(g0,g1)
FEATURE [PartDesign::Pocket] Pocket005
  BaseFeature = -> Pad002
  Direction = (0,1,2e-16)
  Length = 1.4
  Length2 = 5
  Profile = -> Sketch010
  ReferenceAxis = -> Sketch010 [N_Axis]
  Type = 0
FEATURE [Sketcher::SketchObject] Sketch011
  ExternalGeometry = -> [Sketch008,Pocket005]
  FullyConstrained = false
  MapMode = 5
  Placement = pos=(0,-61.9,-1.37e-14) rot=(1,0,0;1.5708rad)
  Support = -> [DatumPlane001]
  sketch-geometry (4):
    g0: Circle CenterX=47 CenterY=36 CenterZ=0 NormalX=0 NormalY=0 NormalZ=1 AngleXU=0 Radius=1.975
    g1: Circle CenterX=47 CenterY=6 CenterZ=0 NormalX=0 NormalY=0 NormalZ=1 AngleXU=0 Radius=1.975
    g2: Circle CenterX=-47 CenterY=6 CenterZ=0 NormalX=0 NormalY=0 NormalZ=1 AngleXU=0 Radius=1.975
    g3: Circle CenterX=-47 CenterY=36 CenterZ=0 NormalX=0 NormalY=0 NormalZ=1 AngleXU=0 Radius=1.975
FEATURE [PartDesign::Pocket] Pocket006
  BaseFeature = -> Pocket005
  Direction = (0,1,2e-16)
  Length = 4
  Length2 = 5
  Profile = -> Sketch011
  ReferenceAxis = -> Sketch011 [N_Axis]
  Type = 0
FEATURE [Sketcher::SketchObject] Sketch012
  FullyConstrained = true
  MapMode = 5
  Placement = pos=(-61.75,0,0) rot=(0.57735,-0.57735,-0.57735;2.0944rad)
  Support = -> [Pocket006]
  sketch-geometry (4):
    g0: LineSegment StartX=-14 StartY=17.5 StartZ=0 EndX=1 EndY=17.5 EndZ=0
    g1: LineSegment StartX=1 StartY=17.5 StartZ=0 EndX=1 EndY=7.5 EndZ=0
    g2: LineSegment StartX=1 StartY=7.5 StartZ=0 EndX=-14 EndY=7.5 EndZ=0
    g3: LineSegment StartX=-14 StartY=7.5 StartZ=0 EndX=-14 EndY=17.5 EndZ=0
  constraints (12):
    c: Coincident(g0,g1)
    c: Coincident(g1,g2)
    c: Coincident(g2,g3)
    c: Coincident(g3,g0)
    c: Horizontal(g0)
    c: Horizontal(g2)
    c: Vertical(g1)
    c: Vertical(g3)
    c: DistanceY(g3,g3) = 10
    c: DistanceX(g0,g0) = 15
    c: DistanceY(g-1,g2) = 7.5
    c: DistanceX(g-1,g1) = 1
FEATURE [Sketcher::SketchObject] Sketch013
  AttachmentOffset = pos=(0,0,2.5) rot=(0,0,1;0rad)
  ExternalGeometry = -> [Sketch012]
  FullyConstrained = true
  MapMode = 5
  Placement = pos=(-64.25,0,0) rot=(0.57735,-0.57735,-0.57735;2.0944rad)
  Support = -> [Pocket006]
  sketch-geometry (6):
    g0: LineSegment StartX=-2.5 StartY=15 StartZ=0 EndX=-2.501 EndY=15 EndZ=0
    g1: LineSegment StartX=-2.501 StartY=15 StartZ=0 EndX=-2.501 EndY=10 EndZ=0
    g2: LineSegment StartX=-2.501 StartY=10 StartZ=0 EndX=-2.5 EndY=10 EndZ=0
    g3: LineSegment StartX=-2.5 StartY=10 StartZ=0 EndX=-2.5 EndY=15 EndZ=0
    g4: LineSegment StartX=1 StartY=17.5 StartZ=0 EndX=-2.5 EndY=15 EndZ=0
    g5: LineSegment StartX=-2.5 StartY=10 StartZ=0 EndX=1 EndY=7.5 EndZ=0
  constraints (16):
    c: Coincident(g0,g1)
    c: Coincident(g1,g2)
    c: Coincident(g2,g3)
    c: Coincident(g3,g0)
    c: Horizontal(g0)
    c: Horizontal(g2)
    c: Vertical(g1)
    c: Vertical(g3)
    c: DistanceX(g0,g-3) = 3.5
    c: DistanceY(g3,g3) = 5
    c: Coincident(g4,g-3)
    c: Coincident(g4,g0)
    c: Coincident(g5,g2)
    c: Coincident(g5,g-3)
    c: Equal(g4,g5)
    c: DistanceX(g2,g2) = 0.001
FEATURE [PartDesign::AdditiveLoft] AdditiveLoft
  BaseFeature = -> Pocket006
  Closed = false
  Profile = -> Sketch012
  Ruled = false
  Sections = -> [Sketch013]
FEATURE [PartDesign::Mirrored] Mirrored
  BaseFeature = -> AdditiveLoft
  MirrorPlane = -> YZ_Plane
  Originals = -> [AdditiveLoft]
  Overlap = 0
FEATURE [Sketcher::SketchObject] Sketch014
  FullyConstrained = true
  MapMode = 5
  Placement = pos=(0,0,0) rot=(1,0,0;1.5708rad)
  Support = -> [XZ_Plane]
  sketch-geometry (4):
    g0: ArcOfCircle CenterX=-61.75 CenterY=14.5 CenterZ=0 NormalX=0 NormalY=0 NormalZ=1 AngleXU=0 Radius=0.75 StartAngle=3e-16 EndAngle=3.14159
    g1: ArcOfCircle CenterX=-61.75 CenterY=10.5 CenterZ=0 NormalX=0 NormalY=0 NormalZ=1 AngleXU=0 Radius=0.75 StartAngle=3.14159 EndAngle=6.28319
    g2: LineSegment StartX=-62.5 StartY=14.5 StartZ=0 EndX=-62.5 EndY=10.5 EndZ=0
    g3: LineSegment StartX=-61 StartY=10.5 StartZ=0 EndX=-61 EndY=14.5 EndZ=0
  constraints (10):
    c: Tangent(g0,g2) = -1.5708
    c: Tangent(g2,g1) = -1.5708
    c: Tangent(g1,g3) = -1.5708
    c: Tangent(g3,g0) = -1.5708
    c: Equal(g0,g1)
    c: Vertical(g2)
    c: DistanceX(g0,g0) = 1.5
    c: DistanceY(g1,g0) = 4
    c: DistanceX(g1,g-1) = 61
    c: DistanceY(g-1,g1) = 10.5
FEATURE [Sketcher::SketchObject] Sketch015
  FullyConstrained = true
  MapMode = 5
  Support = -> [XY_Plane]
  sketch-geometry (2):
    g0: ArcOfCircle CenterX=188 CenterY=0 CenterZ=0 NormalX=0 NormalY=0 NormalZ=1 AngleXU=0 Radius=250 StartAngle=2.42189 EndAngle=3.27972
    g1: LineSegment StartX=0 StartY=0 StartZ=0 EndX=-59.619 EndY=-34.4211 EndZ=0
  constraints (7):
    c: Radius(g0) = 250
    c: DistanceX(g-1,g0) = 188
    c: Horizontal(g-1,g0)
    c: Vertical(g0,g-1)
    c: Coincident(g1,g-1)
    c: Coincident(g1,g0)
    c: Angle(g1,g-1) = 2.61799
FEATURE [PartDesign::SubtractivePipe] SubtractivePipe
  AuxilleryCurvelinear = true
  AuxillerySpineTangent = false
  BaseFeature = -> Mirrored
  Binormal = (0,0,0)
  Mode = 0
  Profile = -> Sketch014
  Spine = -> Sketch015
  SpineTangent = false
  Transformation = 0
  Transition = 0
FEATURE [PartDesign::Plane] DatumPlane002
  Length = 68.7147
  MapMode = 11
  Placement = pos=(-59.3714,-34.3866,14.5) rot=(-0.602152,0.524238,0.602152;2.17589rad)
  ResizeMode = 0
  Support = -> [SubtractivePipe]
  Width = 106.903
FEATURE [Sketcher::SketchObject] Sketch016
  ExternalGeometry = -> [SubtractivePipe]
  FullyConstrained = true
  MapMode = 5
  Placement = pos=(-59.3714,-34.3866,14.5) rot=(-0.602152,0.524238,0.602152;2.17589rad)
  Support = -> [DatumPlane002]
  sketch-geometry (4):
    g0: ArcOfCircle CenterX=0 CenterY=1.42e-14 CenterZ=0 NormalX=0 NormalY=0 NormalZ=1 AngleXU=0 Radius=0.75 StartAngle=1.5708 EndAngle=4.71239
    g1: ArcOfCircle CenterX=4 CenterY=0 CenterZ=0 NormalX=0 NormalY=0 NormalZ=1 AngleXU=0 Radius=0.75 StartAngle=4.71239 EndAngle=7.85398
    g2: LineSegment StartX=1.457e-13 StartY=-0.75 StartZ=0 EndX=4 EndY=-0.75 EndZ=0
    g3: LineSegment StartX=4 StartY=0.75 StartZ=0 EndX=3.122e-13 EndY=0.75 EndZ=0
  constraints (7):
    c: Tangent(g0,g2) = -1.5708
    c: Tangent(g2,g1) = -1.5708
    c: Tangent(g1,g3) = -1.5708
    c: Tangent(g3,g0) = -1.5708
    c: Coincident(g0,g-4)
    c: Coincident(g1,g-3)
    c: Coincident(g1,g-3)
FEATURE [Sketcher::SketchObject] Sketch017
  ExternalGeometry = -> [Sketch006]
  FullyConstrained = true
  MapMode = 5
  Placement = pos=(0,-61.9,-1.37e-14) rot=(1,0,0;1.5708rad)
  Support = -> [DatumPlane001]
  sketch-geometry (1):
    g0: Circle CenterX=-54.5 CenterY=14.5 CenterZ=0 NormalX=0 NormalY=0 NormalZ=1 AngleXU=0 Radius=2
  constraints (2):
    c: Coincident(g0,g-3)
    c: Equal(g0,g-3)
FEATURE [PartDesign::SubtractiveLoft] SubtractiveLoft
  BaseFeature = -> SubtractivePipe
  Closed = false
  Profile = -> Sketch016
  Ruled = false
  Sections = -> [Sketch017]
FEATURE [PartDesign::Plane] DatumPlane003
  AttachmentOffset = pos=(0,0,16.5) rot=(0,0,1;0rad)
  Length = 144.198
  MapMode = 5
  Placement = pos=(0,0,16.5) rot=(0,0,1;0rad)
  ResizeMode = 0
  Support = -> [XY_Plane001]
  Width = 158.707
FEATURE [Sketcher::SketchObject] Sketch018
  FullyConstrained = true
  MapMode = 5
  Placement = pos=(0,0,16.5) rot=(0,0,1;0rad)
  Support = -> [DatumPlane003]
  sketch-geometry (1):
    g0: Circle CenterX=0 CenterY=0 CenterZ=0 NormalX=0 NormalY=0 NormalZ=1 AngleXU=0 Radius=59.5
  constraints (2):
    c: Coincident(g0,g-1)
    c: Diameter(g0) = 119
FEATURE [PartDesign::Pad] Pad003
  Direction = (0,0,1)
  Length = 4
  Length2 = 10
  Midplane = true
  Placement = pos=(0,0,16.5) rot=(0,0,1;0rad)
  Profile = -> Sketch018
  ReferenceAxis = -> Sketch018 [N_Axis]
  Type = 0
FEATURE [PartDesign::Fillet] Fillet
  Base = -> Pad003 [Face1]
  BaseFeature = -> Pad003
  Placement = pos=(0,0,16.5) rot=(0,0,1;0rad)
  Radius = 1.999
  SupportTransform = false
  UseAllEdges = false
FEATURE [PartDesign::Line] DatumLine001
  AttacherType = Attacher::AttachEngineLine
  AttachmentOffset = pos=(0,16.5,0) rot=(0,0,1;0rad)
  Length = 20
  MapMode = 29
  Placement = pos=(0,3.7e-15,16.5) rot=(0,0.707107,0.707107;3.14159rad)
  ResizeMode = 0
  Support = -> [Y_Axis001]
FEATURE [PartDesign::Plane] DatumPlane004
  AttachmentOffset = pos=(0,0,60) rot=(0,0,1;0rad)
  Length = 134.417
  MapMode = 5
  Placement = pos=(0,-60,-1.33e-14) rot=(1,0,0;1.5708rad)
  ResizeMode = 0
  Support = -> [XZ_Plane001]
  Width = 65.4267
FEATURE [Sketcher::SketchObject] Sketch019
  ExternalGeometry = -> [DatumLine001]
  FullyConstrained = true
  MapMode = 5
  Placement = pos=(0,-60,-1.33e-14) rot=(1,0,0;1.5708rad)
  Support = -> [DatumPlane004]
  sketch-geometry (1):
    g0: Circle CenterX=0 CenterY=16.5 CenterZ=0 NormalX=0 NormalY=0 NormalZ=1 AngleXU=0 Radius=4.6
  constraints (2):
    c: Coincident(g0,g-3)
    c: Diameter(g0) = 9.2
FEATURE [PartDesign::Pad] Pad004
  BaseFeature = -> Fillet
  Direction = (0,-1,2e-16)
  Length = 15
  Length2 = 10
  Placement = pos=(0,0,16.5) rot=(0,0,1;0rad)
  Profile = -> Sketch019
  ReferenceAxis = -> Sketch019 [N_Axis]
  Reversed = true
  Type = 0
FEATURE [PartDesign::Mirrored] Mirrored001
  BaseFeature = -> Pad004
  MirrorPlane = -> XZ_Plane001
  Originals = -> [Pad004]
  Overlap = 0
  Placement = pos=(0,0,16.5) rot=(0,0,1;0rad)
FEATURE [Sketcher::SketchObject] Sketch020
  FullyConstrained = true
  MapMode = 5
  Placement = pos=(3.06e-14,-60,16.5) rot=(1,0,0;1.5708rad)
  Support = -> [Mirrored001]
  expr: Constraints[10] = Spreadsheet.MotorShaftCutoutThickness
  expr: Constraints[9] = Spreadsheet.MotorShaftCutoutDiameter
  sketch-geometry (4):
    g0: LineSegment StartX=-2.21077 StartY=1.55 StartZ=0 EndX=2.21077 EndY=1.55 EndZ=0
    g1: LineSegment StartX=-2.21077 StartY=-1.55 StartZ=0 EndX=2.21077 EndY=-1.55 EndZ=0
    g2: ArcOfCircle CenterX=0 CenterY=0 CenterZ=0 NormalX=0 NormalY=0 NormalZ=1 AngleXU=0 Radius=2.7 StartAngle=2.53012 EndAngle=3.75307
    g3: ArcOfCircle CenterX=0 CenterY=0 CenterZ=0 NormalX=0 NormalY=0 NormalZ=1 AngleXU=0 Radius=2.7 StartAngle=5.67171 EndAngle=6.89466
  constraints (11):
    c: Horizontal(g0)
    c: Horizontal(g1)
    c: Coincident(g2,g-1)
    c: Coincident(g2,g0)
    c: Coincident(g2,g1)
    c: Coincident(g3,g2)
    c: Coincident(g3,g1)
    c: Coincident(g3,g0)
    c: Symmetric(g0,g1,g2)
    c: Diameter(g3) = 5.4
    c: DistanceY(g1,g0) = 3.1
FEATURE [PartDesign::Pocket] Pocket007
  BaseFeature = -> Mirrored001
  Direction = (-5e-16,1,-7e-16)
  Length = 10
  Length2 = 5
  Placement = pos=(0,0,16.5) rot=(0,0,1;0rad)
  Profile = -> Sketch020
  ReferenceAxis = -> Sketch020 [N_Axis]
  Type = 0
FEATURE [Sketcher::SketchObject] Sketch021
  FullyConstrained = true
  MapMode = 5
  Placement = pos=(3.06e-14,60,16.5) rot=(0,0.707107,0.707107;3.14159rad)
  Support = -> [Pocket007]
FEATURE [Sketcher::SketchObject] Sketch022
  FullyConstrained = true
  MapMode = 5
  Placement = pos=(3.06e-14,60,16.5) rot=(0,0.707107,0.707107;3.14159rad)
  Support = -> [Pocket007]
  expr: Constraints[1] = Spreadsheet.BearingInsideBoreSize
  sketch-geometry (1):
    g0: Circle CenterX=0 CenterY=0 CenterZ=0 NormalX=0 NormalY=0 NormalZ=1 AngleXU=0 Radius=3
  constraints (2):
    c: Coincident(g0,g-1)
    c: Diameter(g0) = 6
FEATURE [PartDesign::Pad] Pad005
  BaseFeature = -> Pocket007
  Direction = (5e-16,1,7e-16)
  Length = 7.5
  Length2 = 10
  Placement = pos=(0,0,16.5) rot=(0,0,1;0rad)
  Profile = -> Sketch022
  ReferenceAxis = -> Sketch022 [N_Axis]
  Type = 0
FEATURE [Sketcher::SketchObject] Sketch023
  FullyConstrained = true
  MapMode = 5
  Placement = pos=(0,67.5,16.5) rot=(0,0.707107,0.707107;3.14159rad)
  Support = -> [Pad005]
  expr: Constraints[10] = Spreadsheet.PotentiometerPinThickness
  expr: Constraints[9] = Spreadsheet.PotentiometerPinDiameter
  sketch-geometry (4):
    g0: LineSegment StartX=-1.32288 StartY=1.5 StartZ=0 EndX=1.32288 EndY=1.5 EndZ=0
    g1: LineSegment StartX=-1.32288 StartY=-1.5 StartZ=0 EndX=1.32288 EndY=-1.5 EndZ=0
    g2: ArcOfCircle CenterX=0 CenterY=0 CenterZ=0 NormalX=0 NormalY=0 NormalZ=1 AngleXU=0 Radius=2 StartAngle=2.29353 EndAngle=3.98965
    g3: ArcOfCircle CenterX=0 CenterY=0 CenterZ=0 NormalX=0 NormalY=0 NormalZ=1 AngleXU=0 Radius=2 StartAngle=5.43512 EndAngle=7.13125
  constraints (11):
    c: Horizontal(g0)
    c: Horizontal(g1)
    c: Coincident(g2,g-1)
    c: Coincident(g2,g1)
    c: Coincident(g2,g0)
    c: Coincident(g3,g2)
    c: Coincident(g3,g1)
    c: Coincident(g3,g0)
    c: Symmetric(g0,g1,g2)
    c: Diameter(g3) = 4
    c: DistanceY(g1,g0) = 3
FEATURE [PartDesign::Pad] Pad006
  BaseFeature = -> Pad005
  Direction = (0,1,-2e-16)
  Length = 6
  Length2 = 10
  Placement = pos=(0,0,16.5) rot=(0,0,1;0rad)
  Profile = -> Sketch023
  ReferenceAxis = -> Sketch023 [N_Axis]
  Type = 0
FEATURE [PartDesign::Fillet] Fillet001
  Base = -> Pad006 [Edge47,Edge9]
  BaseFeature = -> Pad006
  Placement = pos=(0,0,16.5) rot=(0,0,1;0rad)
  Radius = 1
  SupportTransform = false
  UseAllEdges = false
FEATURE [PartDesign::Chamfer] Chamfer
  Angle = 45
  Base = -> Fillet001 [Edge57,Edge93,Edge77,Edge35]
  BaseFeature = -> Fillet001
  ChamferType = 0
  FlipDirection = false
  Placement = pos=(0,0,16.5) rot=(0,0,1;0rad)
  Size = 2.599
  Size2 = 1
  SupportTransform = false
  UseAllEdges = false
FEATURE [PartDesign::Body] Body001  label="Disc"
  Group = -> [DatumPlane003,Sketch018,Pad003,Fillet,DatumLine001,DatumPlane004,Sketch019,Pad004,Mirrored001,Sketch020,Pocket007,Sketch021,Sketch022,Pad005,Sketch023,Pad006,Fillet001,Chamfer]
  Origin = -> Origin001
  Tip = -> Chamfer
FEATURE [Sketcher::SketchObject] Sketch024
  AttachmentOffset = pos=(0,0,63.9) rot=(0,0,1;0rad)
  FullyConstrained = true
  MapMode = 5
  Placement = pos=(0,-63.9,-1.42e-14) rot=(1,0,0;1.5708rad)
  Support = -> [XZ_Plane002]
  sketch-geometry (13):
    g0: LineSegment StartX=-50 StartY=39 StartZ=0 EndX=-7.41606 EndY=39 EndZ=0
    g1: LineSegment StartX=50 StartY=39 StartZ=0 EndX=50 EndY=3 EndZ=0
    g2: LineSegment StartX=50 StartY=3 StartZ=0 EndX=20.6826 EndY=3 EndZ=0
    g3: LineSegment StartX=-50 StartY=3 StartZ=0 EndX=-50 EndY=39 EndZ=0
    g4: ArcOfCircle CenterX=-3.19 CenterY=35.48 CenterZ=0 NormalX=0 NormalY=0 NormalZ=1 AngleXU=0 Radius=5.5 StartAngle=2.44709 EndAngle=6.97768
    g5: Circle CenterX=0 CenterY=16.5 CenterZ=0 NormalX=0 NormalY=0 NormalZ=1 AngleXU=0 Radius=5.5
    g6: ArcOfCircle CenterX=16.44 CenterY=6.5 CenterZ=0 NormalX=0 NormalY=0 NormalZ=1 AngleXU=0 Radius=5.5 StartAngle=5.59341 EndAngle=10.1146
    g7: LineSegment StartX=1.03606 StartY=39 StartZ=0 EndX=50 EndY=39 EndZ=0
    g8: LineSegment StartX=12.1974 StartY=3 StartZ=0 EndX=-50 EndY=3 EndZ=0
    g9: Circle CenterX=-47 CenterY=36 CenterZ=0 NormalX=0 NormalY=0 NormalZ=1 AngleXU=0 Radius=1.7
    g10: Circle CenterX=-47 CenterY=6 CenterZ=0 NormalX=0 NormalY=0 NormalZ=1 AngleXU=0 Radius=1.7
    g11: Circle CenterX=47 CenterY=36 CenterZ=0 NormalX=0 NormalY=0 NormalZ=1 AngleXU=0 Radius=1.7
    g12: Circle CenterX=47 CenterY=6 CenterZ=0 NormalX=0 NormalY=0 NormalZ=1 AngleXU=0 Radius=1.7
  constraints (39):
    c: Coincident(g7,g1)
    c: Coincident(g1,g2)
    c: Coincident(g8,g3)
    c: Coincident(g3,g0)
    c: Horizontal(g0)
    c: Vertical(g1)
    c: Vertical(g3)
    c: DistanceX(g0,g7) = 100
    c: DistanceY(g1,g1) = 36
    c: DistanceY(g-1,g1) = 3
    c: Symmetric(g1,g8,g-2)
    c: Diameter(g4) = 11
    c: DistanceX(g4,g-1) = 3.19
    c: DistanceY(g-1,g4) = 35.48
    c: PointOnObject(g5,g-2)
    c: Equal(g5,g6)
    c: Equal(g6,g4)
    c: DistanceY(g-1,g5) = 16.5
    c: DistanceY(g-1,g6) = 6.5
    c: DistanceX(g-1,g6) = 16.44
    c: Coincident(g0,g4)
    c: Coincident(g7,g4)
    c: Coincident(g2,g6)
    c: Coincident(g8,g6)
    c: Equal(g1,g3)
    c: Horizontal(g7)
    c: Horizontal(g2)
    c: Horizontal(g8)
    c: Diameter(g9) = 3.4
    c: Equal(g9,g10)
    c: Equal(g10,g12)
    c: Equal(g12,g11)
    c: Vertical(g9,g10)
    c: Vertical(g11,g12)
    c: Horizontal(g11,g9)
    c: DistanceX(g9,g11) = 94
    c: DistanceY(g10,g9) = 30
    c: Symmetric(g10,g12,g-2)
    c: DistanceY(g-1,g12) = 6
FEATURE [PartDesign::Pad] Pad007
  Direction = (0,-1,2e-16)
  Length = 1.6
  Length2 = 10
  Placement = pos=(0,0,0) rot=(1,0,0;1.5708rad)
  Profile = -> Sketch024
  ReferenceAxis = -> Sketch024 [N_Axis]
  Type = 0
FEATURE [PartDesign::Body] Body002  label="PCB"
  Group = -> [Sketch024,Pad007]
  Origin = -> Origin002
  Tip = -> Pad007
FEATURE [PartDesign::Chamfer] Chamfer001
  Angle = 45
  Base = -> SubtractiveLoft [Edge392,Edge388,Edge387,Edge365,Edge369,Edge372]
  BaseFeature = -> SubtractiveLoft
  ChamferType = 0
  FlipDirection = false
  Size = 1.999
  Size2 = 1
  SupportTransform = false
  UseAllEdges = false
FEATURE [TechDraw::DrawSVGTemplate] Template
  EditableTexts = AUTHOR_NAME=Kristof Robberechts; DN=DN; DRAWING_TITLE=OpenDucoValve PCB; FC-DATE=06/04/2022; FC-REV=REV A; FC-SC=2:1; FC-SH=1 / 1; FC-SI=A4; FreeCAD_DRAWING=FreeCAD DRAWING; PN=PN
  Height = 210
  Orientation = 1
  Width = 297
FEATURE [TechDraw::DrawViewPart] View  label="Front View"
  CoarseView = false
  Direction = (0,-1,0)
  Focus = 100
  HardHidden = false
  IsoCount = 0
  IsoHidden = false
  IsoVisible = false
  LockPosition = false
  Perspective = false
  Rotation = 0
  Scale = 2
  ScaleType = 0
  SeamHidden = false
  SeamVisible = true
  SmoothHidden = false
  SmoothVisible = true
  Source = -> [Body002]
  X = 148.353
  XDirection = (1,0,0)
  Y = 116.386
FEATURE [TechDraw::DrawViewDimension] Dimension
  AngleOverride = false
  Arbitrary = false
  ArbitraryTolerances = false
  EqualTolerance = true
  ExtensionAngle = 0
  FormatSpec = %.2w
  FormatSpecOverTolerance = %+.2w
  FormatSpecUnderTolerance = %+.2w
  Inverted = false
  LineAngle = 0
  LockPosition = false
  MeasureType = 1
  OverTolerance = 0
  References2D = -> [View]
  Rotation = 0
  ScaleType = 0
  TheoreticalExact = false
  Type = 1
  UnderTolerance = 0
  X = -3.56663
  Y = 63.571
FEATURE [TechDraw::DrawViewDimension] Dimension001
  AngleOverride = false
  Arbitrary = false
  ArbitraryTolerances = false
  EqualTolerance = true
  ExtensionAngle = 0
  FormatSpec = %.2w
  FormatSpecOverTolerance = %+.2w
  FormatSpecUnderTolerance = %+.2w
  Inverted = false
  LineAngle = 0
  LockPosition = false
  MeasureType = 1
  OverTolerance = 0
  References2D = -> [View]
  Rotation = 0
  ScaleType = 0
  TheoreticalExact = false
  Type = 2
  UnderTolerance = 0
  X = -129.945
  Y = 2.5
FEATURE [TechDraw::DrawViewDimension] Dimension003
  AngleOverride = false
  Arbitrary = false
  ArbitraryTolerances = false
  EqualTolerance = true
  ExtensionAngle = 0
  FormatSpec = ⌀%.2w
  FormatSpecOverTolerance = %+.2w
  FormatSpecUnderTolerance = %+.2w
  Inverted = false
  LineAngle = 0
  LockPosition = false
  MeasureType = 1
  OverTolerance = 0
  References2D = -> [View]
  Rotation = 0
  ScaleType = 0
  TheoreticalExact = false
  Type = 5
  UnderTolerance = 0
  X = 19.1204
  Y = 45.8071
FEATURE [TechDraw::DrawViewDimension] Dimension004
  AngleOverride = false
  Arbitrary = false
  ArbitraryTolerances = false
  EqualTolerance = true
  ExtensionAngle = 0
  FormatSpec = ⌀%.2w
  FormatSpecOverTolerance = %+.2w
  FormatSpecUnderTolerance = %+.2w
  Inverted = false
  LineAngle = 0
  LockPosition = false
  MeasureType = 1
  OverTolerance = 0
  References2D = -> [View]
  Rotation = 0
  ScaleType = 0
  TheoreticalExact = false
  Type = 5
  UnderTolerance = 0
  X = 18.2342
  Y = 1.53372
FEATURE [TechDraw::DrawViewDimension] Dimension005
  AngleOverride = false
  Arbitrary = false
  ArbitraryTolerances = false
  EqualTolerance = true
  ExtensionAngle = 0
  FormatSpec = ⌀%.2w
  FormatSpecOverTolerance = %+.2w
  FormatSpecUnderTolerance = %+.2w
  Inverted = false
  LineAngle = 0
  LockPosition = false
  MeasureType = 1
  OverTolerance = 0
  References2D = -> [View]
  Rotation = 0
  ScaleType = 0
  TheoreticalExact = false
  Type = 5
  UnderTolerance = 0
  X = 49.1813
  Y = -36.7752
FEATURE [TechDraw::DrawViewDimension] Dimension006
  AngleOverride = false
  Arbitrary = false
  ArbitraryTolerances = false
  EqualTolerance = true
  ExtensionAngle = 0
  FormatSpec = %.2w
  FormatSpecOverTolerance = %+.2w
  FormatSpecUnderTolerance = %+.2w
  Inverted = false
  LineAngle = 0
  LockPosition = false
  MeasureType = 1
  OverTolerance = 0
  References2D = -> [View]
  Rotation = 0
  ScaleType = 0
  TheoreticalExact = false
  Type = 2
  UnderTolerance = 0
  X = -112.304
  Y = 2.38675
FEATURE [TechDraw::DrawViewDimension] Dimension007
  AngleOverride = false
  Arbitrary = false
  ArbitraryTolerances = false
  EqualTolerance = true
  ExtensionAngle = 0
  FormatSpec = %.2w
  FormatSpecOverTolerance = %+.2w
  FormatSpecUnderTolerance = %+.2w
  Inverted = false
  LineAngle = 0
  LockPosition = false
  MeasureType = 1
  OverTolerance = 0
  References2D = -> [View]
  Rotation = 0
  ScaleType = 0
  TheoreticalExact = false
  Type = 1
  UnderTolerance = 0
  X = -3.49462
  Y = 53.4677
FEATURE [TechDraw::DrawViewDimension] Dimension010
  AngleOverride = false
  Arbitrary = false
  ArbitraryTolerances = false
  EqualTolerance = true
  ExtensionAngle = 0
  FormatSpec = %.2w
  FormatSpecOverTolerance = %+.2w
  FormatSpecUnderTolerance = %+.2w
  Inverted = false
  LineAngle = 0
  LockPosition = false
  MeasureType = 1
  OverTolerance = 0
  References2D = -> [View]
  Rotation = 0
  ScaleType = 0
  TheoreticalExact = false
  Type = 1
  UnderTolerance = 0
  X = -24.9642
  Y = 31.4621
FEATURE [TechDraw::DrawViewDimension] Dimension011
  AngleOverride = false
  Arbitrary = false
  ArbitraryTolerances = false
  EqualTolerance = true
  ExtensionAngle = 0
  FormatSpec = %.2w
  FormatSpecOverTolerance = %+.2w
  FormatSpecUnderTolerance = %+.2w
  Inverted = false
  LineAngle = 0
  LockPosition = false
  MeasureType = 1
  OverTolerance = 0
  References2D = -> [View]
  Rotation = 0
  ScaleType = 0
  TheoreticalExact = false
  Type = 1
  UnderTolerance = 0
  X = -15.2778
  Y = -0.062724
FEATURE [TechDraw::DrawViewDimension] Dimension012
  AngleOverride = false
  Arbitrary = false
  ArbitraryTolerances = false
  EqualTolerance = true
  ExtensionAngle = 0
  FormatSpec = %.2w
  FormatSpecOverTolerance = %+.2w
  FormatSpecUnderTolerance = %+.2w
  Inverted = false
  LineAngle = 0
  LockPosition = false
  MeasureType = 1
  OverTolerance = 0
  References2D = -> [View]
  Rotation = 0
  ScaleType = 0
  TheoreticalExact = false
  Type = 1
  UnderTolerance = 0
  X = 13.707
  Y = -28.2079
FEATURE [TechDraw::DrawViewDimension] Dimension013
  AngleOverride = false
  Arbitrary = false
  ArbitraryTolerances = false
  EqualTolerance = true
  ExtensionAngle = 0
  FormatSpec = %.2w
  FormatSpecOverTolerance = %+.2w
  FormatSpecUnderTolerance = %+.2w
  Inverted = false
  LineAngle = 0
  LockPosition = false
  MeasureType = 1
  OverTolerance = 0
  References2D = -> [View]
  Rotation = 0
  ScaleType = 0
  TheoreticalExact = false
  Type = 2
  UnderTolerance = 0
  X = -16.4606
  Y = 17.7972
FEATURE [TechDraw::DrawViewDimension] Dimension014
  AngleOverride = false
  Arbitrary = false
  ArbitraryTolerances = false
  EqualTolerance = true
  ExtensionAngle = 0
  FormatSpec = %.2w
  FormatSpecOverTolerance = %+.2w
  FormatSpecUnderTolerance = %+.2w
  Inverted = false
  LineAngle = 0
  LockPosition = false
  MeasureType = 1
  OverTolerance = 0
  References2D = -> [View]
  Rotation = 0
  ScaleType = 0
  TheoreticalExact = false
  Type = 2
  UnderTolerance = 0
  X = -6.94444
  Y = -22.0161
FEATURE [TechDraw::DrawViewDimension] Dimension015
  AngleOverride = false
  Arbitrary = false
  ArbitraryTolerances = false
  EqualTolerance = true
  ExtensionAngle = 0
  FormatSpec = %.2w
  FormatSpecOverTolerance = %+.2w
  FormatSpecUnderTolerance = %+.2w
  Inverted = false
  LineAngle = 0
  LockPosition = false
  MeasureType = 1
  OverTolerance = 0
  References2D = -> [View]
  Rotation = 0
  ScaleType = 0
  TheoreticalExact = false
  Type = 2
  UnderTolerance = 0
  X = 54.0204
  Y = -17.4942
FEATURE [TechDraw::DrawViewDimension] Dimension016
  AngleOverride = false
  Arbitrary = false
  ArbitraryTolerances = false
  EqualTolerance = true
  ExtensionAngle = 0
  FormatSpec = ⌀%.2w
  FormatSpecOverTolerance = %+.2w
  FormatSpecUnderTolerance = %+.2w
  Inverted = false
  LineAngle = 0
  LockPosition = false
  MeasureType = 1
  OverTolerance = 0
  References2D = -> [View]
  Rotation = 0
  ScaleType = 0
  TheoreticalExact = false
  Type = 5
  UnderTolerance = 0
  X = 109.855
  Y = 35.2551
FEATURE [TechDraw::DrawViewDimension] Dimension017
  AngleOverride = false
  Arbitrary = false
  ArbitraryTolerances = false
  EqualTolerance = true
  ExtensionAngle = 0
  FormatSpec = %.2w
  FormatSpecOverTolerance = %+.2w
  FormatSpecUnderTolerance = %+.2w
  Inverted = false
  LineAngle = 0
  LockPosition = false
  MeasureType = 1
  OverTolerance = 0
  References2D = -> [View]
  Rotation = 0
  ScaleType = 0
  TheoreticalExact = false
  Type = 1
  UnderTolerance = 0
  X = 107.225
  Y = -14.2077
FEATURE [TechDraw::DrawViewDimension] Dimension018
  AngleOverride = false
  Arbitrary = false
  ArbitraryTolerances = false
  EqualTolerance = true
  ExtensionAngle = 0
  FormatSpec = %.2w
  FormatSpecOverTolerance = %+.2w
  FormatSpecUnderTolerance = %+.2w
  Inverted = false
  LineAngle = 0
  LockPosition = false
  MeasureType = 1
  OverTolerance = 0
  References2D = -> [View]
  Rotation = 0
  ScaleType = 0
  TheoreticalExact = false
  Type = 2
  UnderTolerance = 0
  X = 83.9797
  Y = -41.3383
FEATURE [TechDraw::DrawPage] Page  label="PCB Drawing"
  KeepUpdated = true
  NextBalloonIndex = 1
  ProjectionType = 0
  Template = -> Template
  Views = -> [View,Dimension,Dimension001,Dimension003,Dimension004,Dimension005,Dimension006,Dimension007,Dimension010,Dimension011,Dimension012,Dimension013,Dimension014,Dimension015,Dimension016,Dimension017,Dimension018]
FEATURE [Sketcher::SketchObject] Sketch025
  ExternalGeometry = -> [Sketch006]
  FullyConstrained = true
  MapMode = 5
  Placement = pos=(0,-61.9,-1.37e-14) rot=(1,0,0;1.5708rad)
  Support = -> [DatumPlane001]
  sketch-geometry (1):
    g0: Circle CenterX=-54.5 CenterY=27.5 CenterZ=0 NormalX=0 NormalY=0 NormalZ=1 AngleXU=0 Radius=2
  constraints (2):
    c: Coincident(g0,g-3)
    c: Equal(g-3,g0)
FEATURE [Sketcher::SketchObject] Sketch026
  AttachmentOffset = pos=(0,0,27.5) rot=(0,0,1;0rad)
  ExternalGeometry = -> [Sketch025]
  FullyConstrained = false
  MapMode = 5
  Placement = pos=(0,0,27.5) rot=(0,0,1;0rad)
  Support = -> [XY_Plane]
  sketch-geometry (2):
    g0: ArcOfCircle CenterX=-45 CenterY=-61.9 CenterZ=0 NormalX=0 NormalY=0 NormalZ=1 AngleXU=0 Radius=10 StartAngle=0.996019 EndAngle=4.71239
    g1: ArcOfCircle CenterX=-25.5681 CenterY=-31.9 CenterZ=0 NormalX=0 NormalY=0 NormalZ=1 AngleXU=0 Radius=25.7435 StartAngle=4.13761 EndAngle=6.16639
  constraints (7):
    c: Tangent(g1,g0) = 1.5708
    c: PointOnObject(g1,g-2)
    c: DistanceY(g0,g1) = 30
    c: Horizontal(g0,g-3)
    c: DistanceX(g-3,g0) = 7.5
    c: Radius(g0) = 10
    c: Vertical(g0,g0)
FEATURE [PartDesign::SubtractivePipe] SubtractivePipe001
  AuxilleryCurvelinear = true
  AuxillerySpineTangent = false
  BaseFeature = -> Chamfer001
  Binormal = (0,0,0)
  Mode = 0
  Profile = -> Sketch025
  Spine = -> Sketch026
  SpineTangent = false
  Transformation = 0
  Transition = 0
FEATURE [PartDesign::Body] Body  label="ValveBody"
  Group = -> [Sketch,Pad,Sketch001,Pocket,DatumPlane,Sketch002,Pocket001,Sketch003,Pocket002,Sketch004,Pocket003,DatumPlane001,Sketch006,Sketch007,Pocket004,Sketch008,Pad001,Sketch009,Pad002,Sketch010,Pocket005,Sketch011,Pocket006,Sketch012,Sketch013,AdditiveLoft,Mirrored,Sketch014,Sketch015,SubtractivePipe,DatumPlane002,Sketch016,Sketch017,SubtractiveLoft,DatumLine,Chamfer001,Sketch025,Sketch026,+1 more]
  Origin = -> Origin
  Tip = -> SubtractivePipe001
